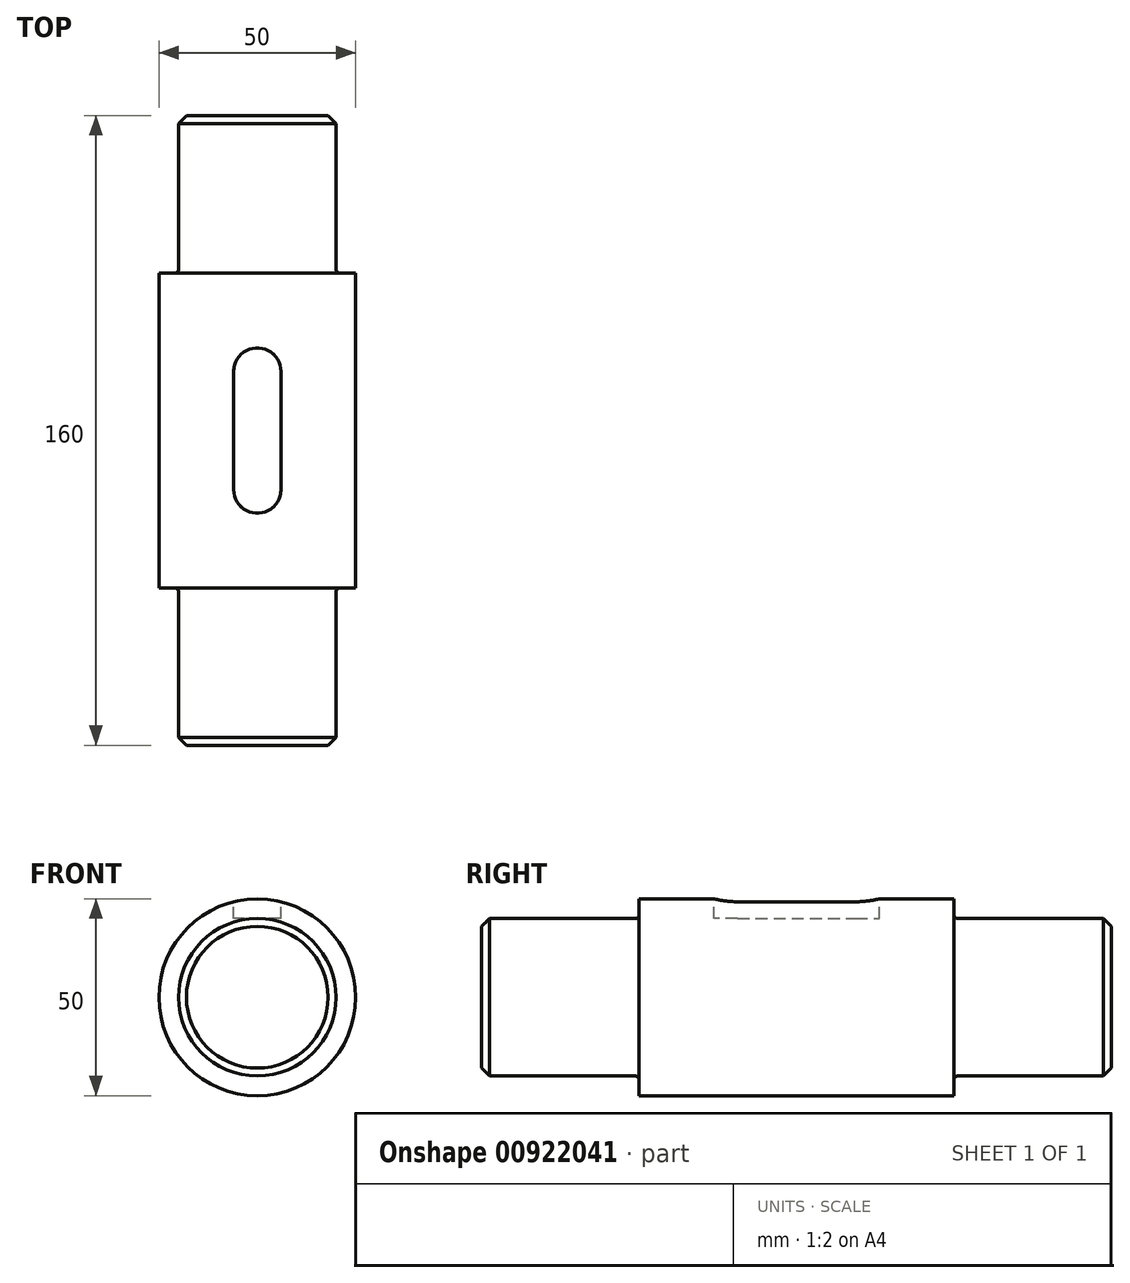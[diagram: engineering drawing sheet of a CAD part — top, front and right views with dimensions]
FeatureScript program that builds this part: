
annotation { "Feature Type Name" : "Feature", "Feature Type Description" : "" }
export const myFeature = defineFeature(function(context is Context, id is Id, definition is map)
    precondition{}
    {
        {
            var Q0;
            Q0=qCreatedBy(makeId("Right.planeOp"),FACE);
            var sketch = newSketch(context, id + "F0", { "sketchPlane" : qUnion([Q0])});
            skLineSegment(sketch, "E0", {"start": v(-40, 25) * mm, "end": v(0, 25) * mm});
            skLineSegment(sketch, "E1", {"start": v(-40, 25) * mm, "end": v(-40, 20) * mm});
            skLineSegment(sketch, "E2", {"start": v(-40, 20) * mm, "end": v(-80, 20) * mm});
            skLineSegment(sketch, "E3", {"start": v(-80, 20) * mm, "end": v(-80, 0) * mm});
            skLineSegment(sketch, "E4.MirrorCS", {"start": v(40, 25) * mm, "end": v(0, 25) * mm});
            skLineSegment(sketch, "E5.MirrorCS", {"start": v(40, 25) * mm, "end": v(40, 20) * mm});
            skLineSegment(sketch, "E6.MirrorCS", {"start": v(40, 20) * mm, "end": v(80, 20) * mm});
            skLineSegment(sketch, "E7.MirrorCS", {"start": v(80, 20) * mm, "end": v(80, 0) * mm});
            skLineSegment(sketch, "E8", {"start": v(-89.03, 0) * mm, "end": v(92.16, 0) * mm});
            skSolve(sketch);
        }
        {
            var Q0;
            Q0 = qSketchRegion(id + "F0", true);
            var Q1;
            Q1=sQuery(id+"F0.wireOp",EDGE,"E8");
            revolve(context, id + "F1", {"surfaceOperationType" : NewSurfaceOperationType.NEW, "entities" : qUnion([Q0]), "axis" : qUnion([Q1]), "revolveType" : RevolveType.FULL});
        }
        {
            var Q0;
            Q0=makeQuery(id+"F1.opRevolve","SWEPT_EDGE",EDGE,{"disambiguationData":[OSD([sQuery(id+"F0.wireOp",EDGE,"E2"),sQuery(id+"F0.wireOp",EDGE,"E3")])]});
            var Q1;
            Q1=makeQuery(id+"F1.opRevolve","SWEPT_EDGE",EDGE,{"disambiguationData":[OSD([sQuery(id+"F0.wireOp",EDGE,"E6.MirrorCS"),sQuery(id+"F0.wireOp",EDGE,"E7.MirrorCS")])]});
            chamfer(context, id + "F2", {"entities" : qUnion([Q0, Q1]), "width" : 2 * mm, "tangentPropagation" : true});
        }
        {
            var Q0;
            Q0=makeQuery(id+"F1.opRevolve","SWEPT_EDGE",EDGE,{"disambiguationData":[OSD([sQuery(id+"F0.wireOp",EDGE,"E1"),sQuery(id+"F0.wireOp",EDGE,"E2")])]});
            fillet(context, id + "F3", {"entities" : qUnion([Q0]), "radius" : 1 * mm, "tangentPropagation" : true, "allowEdgeOverflow" : false});
        }
        {
            var Q0;
            Q0=makeQuery(id+"F1.opRevolve","SWEPT_EDGE",EDGE,{"disambiguationData":[OSD([sQuery(id+"F0.wireOp",EDGE,"E5.MirrorCS"),sQuery(id+"F0.wireOp",EDGE,"E6.MirrorCS")])]});
            fillet(context, id + "F4", {"entities" : qUnion([Q0]), "radius" : 1 * mm, "tangentPropagation" : true, "allowEdgeOverflow" : false});
        }
        {
            var Q0;
            Q0=qCreatedBy(makeId("Top.planeOp"),FACE);
            cPlane(context, id + "F5", {"entities" : qUnion([Q0]), "cplaneType" : CPlaneType.OFFSET, "offset" : 25 * mm, "width" : 150 * mm, "height" : 150 * mm});
        }
        {
            var Q0;
            Q0=qCreatedBy(id+"F5.planeOp",FACE);
            var sketch = newSketch(context, id + "F6", { "sketchPlane" : qUnion([Q0])});
            skLineSegment(sketch, "E9.right", {"start": v(-6, 0) * mm, "end": v(-6, 15) * mm});
            skLineSegment(sketch, "E10.MirrorCS", {"start": v(6, 0) * mm, "end": v(6, 15) * mm});
            skLineSegment(sketch, "E11.MirrorCS", {"start": v(6, 0) * mm, "end": v(6, -15) * mm});
            skLineSegment(sketch, "E12.MirrorCS", {"start": v(-6, 0) * mm, "end": v(-6, -15) * mm});
            skArc(sketch, "E13", {"start": v(6, 15) * mm, "mid": v(0, 21) * mm, "end": v(-6, 15) * mm});
            skArc(sketch, "E14", {"start": v(-6, -15) * mm, "mid": v(0, -21) * mm, "end": v(6, -15) * mm});
            skSolve(sketch);
        }
        {
            var Q0;
            Q0 = qSketchRegion(id + "F6", true);
            extrude(context, id + "F7", {"entities" : qUnion([Q0]), "operationType" : NewBodyOperationType.REMOVE, "oppositeDirection" : true, "depth" : 5 * mm, "offsetDistance" : 25 * mm});
        }
    });
